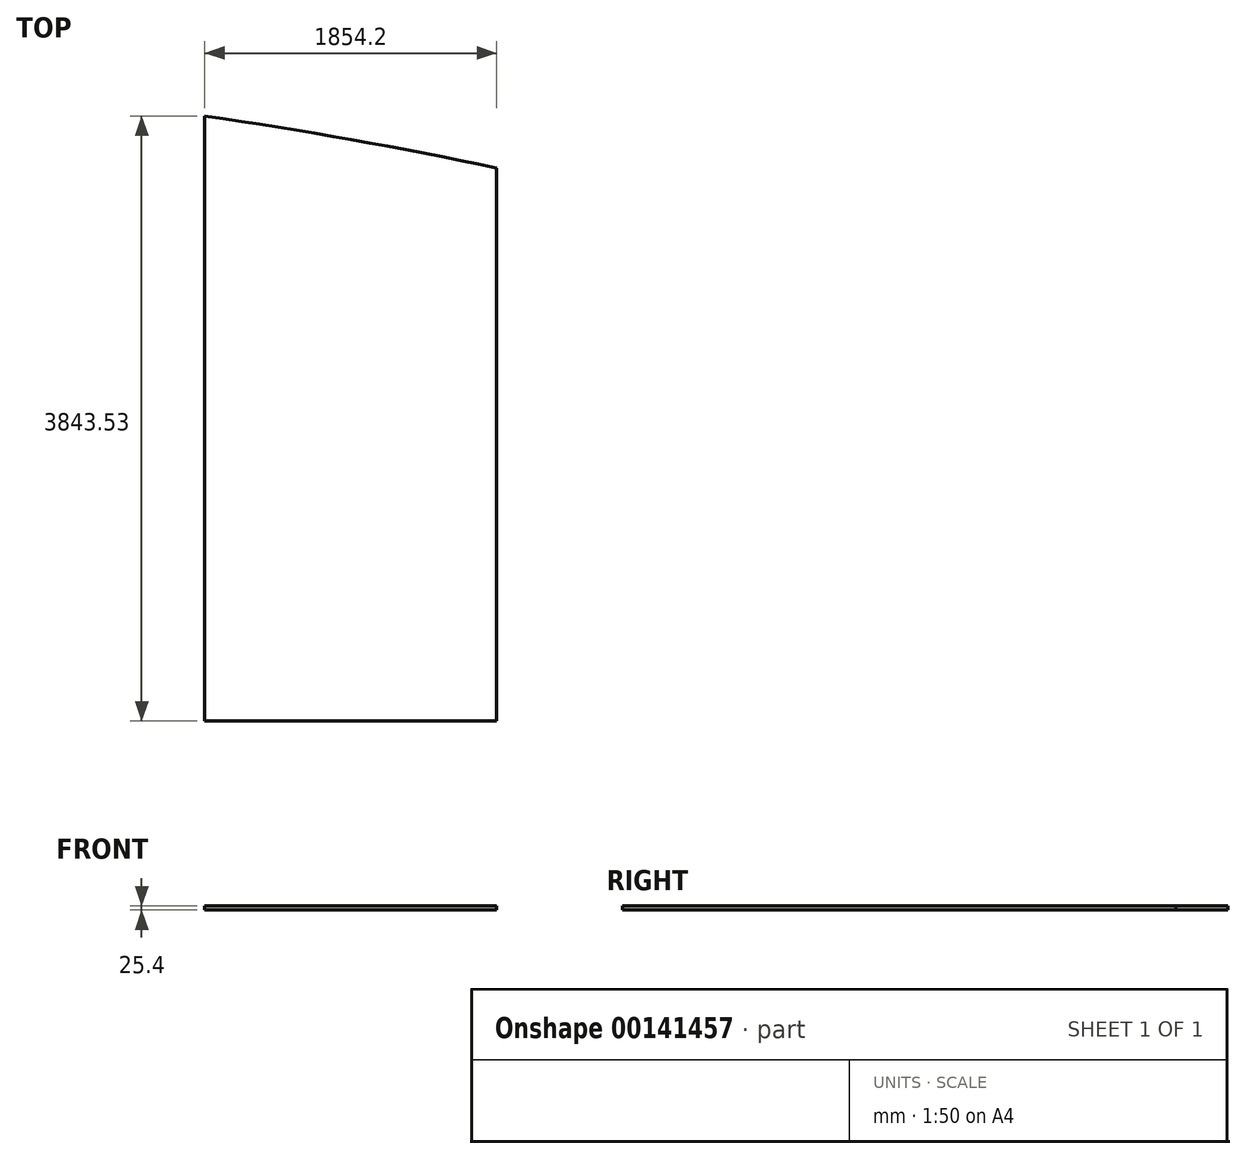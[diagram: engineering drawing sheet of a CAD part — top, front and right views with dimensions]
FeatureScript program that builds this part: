
annotation { "Feature Type Name" : "Feature", "Feature Type Description" : "" }
export const myFeature = defineFeature(function(context is Context, id is Id, definition is map)
    precondition{}
    {
        {
            var Q0;
            Q0=qCreatedBy(makeId("Top.planeOp"),FACE);
            var sketch = newSketch(context, id + "F0", { "sketchPlane" : qUnion([Q0])});
            skLineSegment(sketch, "E0", {"start": v(-954.36, -1720.8) * mm, "end": v(899.84, -1720.8) * mm});
            skLineSegment(sketch, "E1", {"start": v(-954.36, -1720.8) * mm, "end": v(-954.36, 2122.73) * mm});
            skLineSegment(sketch, "E2", {"start": v(899.84, -1720.8) * mm, "end": v(899.84, 1792.78) * mm});
            skLineSegment(sketch, "E3", {"start": v(-27.26, -1720.8) * mm, "end": v(-27.26, 1971.85) * mm});
            skArc(sketch, "E4", {"start": v(899.84, 1792.78) * mm, "mid": v(-24.83, 1971.42) * mm, "end": v(-954.36, 2122.73) * mm});
            skSolve(sketch);
        }
        {
            var Q0;
            {var subQ0=sQuery(id+"F0.wireOp",EDGE,"E1");Q0=makeQuery(id+"F0.imprint","IMPRINT",FACE,{"disambiguationData":[TD([[makeQuery(id+"F0.imprint","IMPRINT",EDGE,{"derivedFrom":subQ0}),-1.0]])]});}
            var Q1;
            {var subQ0=sQuery(id+"F0.wireOp",EDGE,"E2");Q1=makeQuery(id+"F0.imprint","IMPRINT",FACE,{"disambiguationData":[TD([[makeQuery(id+"F0.imprint","IMPRINT",EDGE,{"derivedFrom":subQ0}),1.0]])]});}
            extrude(context, id + "F1", {"entities" : qUnion([Q0, Q1]), "depth" : 25.4 * mm});
        }
    });
